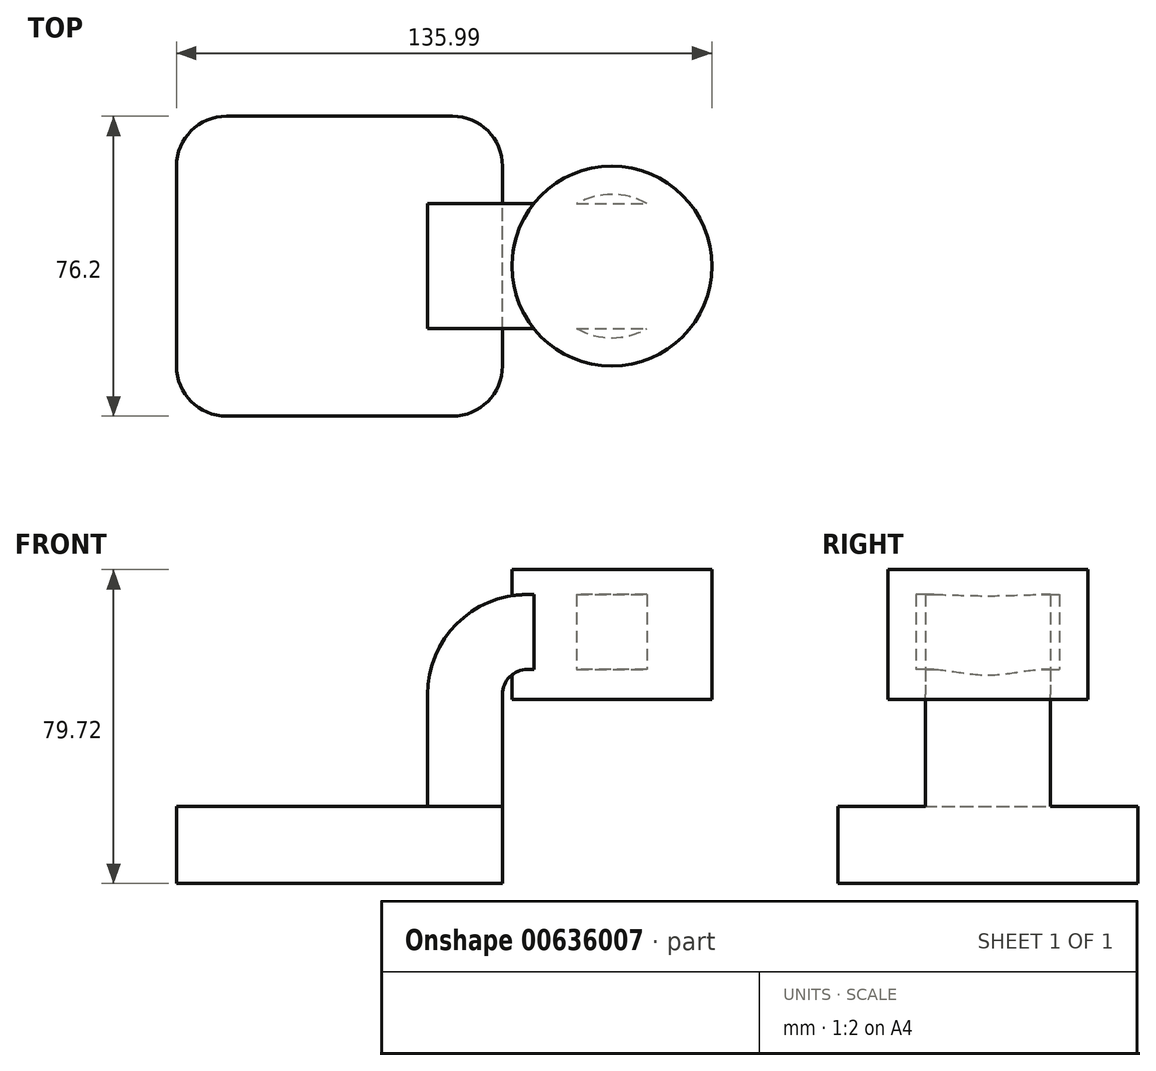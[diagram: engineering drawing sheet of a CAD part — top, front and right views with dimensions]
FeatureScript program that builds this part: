
annotation { "Feature Type Name" : "Feature", "Feature Type Description" : "" }
export const myFeature = defineFeature(function(context is Context, id is Id, definition is map)
    precondition{}
    {
        {
            var Q0;
            Q0=qCreatedBy(makeId("Front.planeOp"),FACE);
            var sketch = newSketch(context, id + "F0", { "sketchPlane" : qUnion([Q0])});
            skLineSegment(sketch, "E0.bottom", {"start": v(41.4, -9.8) * mm, "end": v(-41.4, -9.8) * mm});
            skLineSegment(sketch, "E0.top", {"start": v(41.4, 9.8) * mm, "end": v(-41.4, 9.8) * mm});
            skLineSegment(sketch, "E0.left", {"start": v(41.4, -9.8) * mm, "end": v(41.4, 9.8) * mm});
            skLineSegment(sketch, "E0.right", {"start": v(-41.4, -9.8) * mm, "end": v(-41.4, 9.8) * mm});
            skPoint(sketch, "E0.middle", {"position": v(0, 0) * mm});
            skLineSegment(sketch, "E1.bottom", {"start": v(94.6, 36.9) * mm, "end": v(69.2, 36.9) * mm});
            skLineSegment(sketch, "E1.top", {"start": v(94.6, 69.92) * mm, "end": v(69.2, 69.92) * mm});
            skLineSegment(sketch, "E1.left", {"start": v(94.6, 36.9) * mm, "end": v(94.6, 69.92) * mm});
            skLineSegment(sketch, "E1.right", {"start": v(69.2, 36.9) * mm, "end": v(69.2, 69.92) * mm});
            skPoint(sketch, "E1.middle", {"position": v(81.9, 53.42) * mm});
            skLineSegment(sketch, "E2", {"start": v(41.4, 9.8) * mm, "end": v(41.4, 38.17) * mm});
            skArc(sketch, "E3", {"start": v(41.4, 38.17) * mm, "mid": v(43.26, 42.66) * mm, "end": v(47.75, 44.52) * mm});
            skLineSegment(sketch, "E4", {"start": v(47.75, 44.52) * mm, "end": v(87.41, 44.52) * mm});
            skLineSegment(sketch, "E5.0", {"start": v(47.75, 63.57) * mm, "end": v(87.41, 63.57) * mm});
            skArc(sketch, "E5.1", {"start": v(22.35, 38.17) * mm, "mid": v(29.79, 56.14) * mm, "end": v(47.75, 63.57) * mm});
            skLineSegment(sketch, "E5.2", {"start": v(22.35, 9.8) * mm, "end": v(22.35, 38.17) * mm});
            skLineSegment(sketch, "E6", {"start": v(87.41, 63.57) * mm, "end": v(87.41, 44.52) * mm});
            skSolve(sketch);
        }
        {
            var Q0;
            Q0=makeQuery(id+"F0.imprint","IMPRINT",FACE,{"disambiguationData":[TD([[makeQuery(id+"F0.imprint","IMPRINT",EDGE,{"derivedFrom":sQuery(id+"F0.wireOp",EDGE,"E0.bottom")}),-1.0]])]});
            extrude(context, id + "F1", {"entities" : qUnion([Q0]), "endBound" : BoundingType.SYMMETRIC, "depth" : 76.2 * mm, "offsetDistance" : 25.4 * mm});
        }
        {
            var Q0;
            {var subQ1=sQuery(id+"F0.wireOp",EDGE,"E2");Q0=makeQuery(id+"F0.imprint","IMPRINT",FACE,{"disambiguationData":[TD([[makeQuery(id+"F0.imprint","IMPRINT",EDGE,{"derivedFrom":subQ1}),1.0]])]});}
            var Q1;
            {var subQ5=sQuery(id+"F0.wireOp",EDGE,"E6");Q1=makeQuery(id+"F0.imprint","IMPRINT",FACE,{"disambiguationData":[TD([[makeQuery(id+"F0.imprint","IMPRINT",EDGE,{"derivedFrom":subQ5}),-1.0]])]});}
            extrude(context, id + "F2", {"entities" : qUnion([Q0, Q1]), "operationType" : NewBodyOperationType.ADD, "endBound" : BoundingType.SYMMETRIC, "depth" : 31.75 * mm, "offsetDistance" : 25.4 * mm});
        }
        {
            var Q0;
            {var subQ1=sQuery(id+"F0.wireOp",EDGE,"E1.bottom");Q0=makeQuery(id+"F0.imprint","IMPRINT",FACE,{"disambiguationData":[TD([[makeQuery(id+"F0.imprint","IMPRINT",EDGE,{"derivedFrom":subQ1}),-1.0]])]});}
            var Q1;
            Q1=sQuery(id+"F0.wireOp",EDGE,"E1.right");
            revolve(context, id + "F3", {"operationType" : NewBodyOperationType.ADD, "entities" : qUnion([Q0]), "axis" : qUnion([Q1]), "revolveType" : RevolveType.FULL});
        }
        {
            var Q0;
            Q0=makeQuery(id+"F1.opExtrude","CAP_EDGE",EDGE,{"disambiguationData":[OSD([sQuery(id+"F0.wireOp",EDGE,"E0.right")])],"isStart":false});
            var Q1;
            Q1=makeQuery(id+"F1.opExtrude","CAP_EDGE",EDGE,{"disambiguationData":[OSD([sQuery(id+"F0.wireOp",EDGE,"E0.left")])],"isStart":false});
            var Q2;
            Q2=makeQuery(id+"F1.opExtrude","CAP_EDGE",EDGE,{"disambiguationData":[OSD([sQuery(id+"F0.wireOp",EDGE,"E0.right")])],"isStart":true});
            var Q3;
            Q3=makeQuery(id+"F1.opExtrude","CAP_EDGE",EDGE,{"disambiguationData":[OSD([sQuery(id+"F0.wireOp",EDGE,"E0.left")])],"isStart":true});
            fillet(context, id + "F4", {"entities" : qUnion([Q0, Q1, Q2, Q3]), "radius" : 12.7 * mm, "tangentPropagation" : true, "allowEdgeOverflow" : false});
        }
    });
